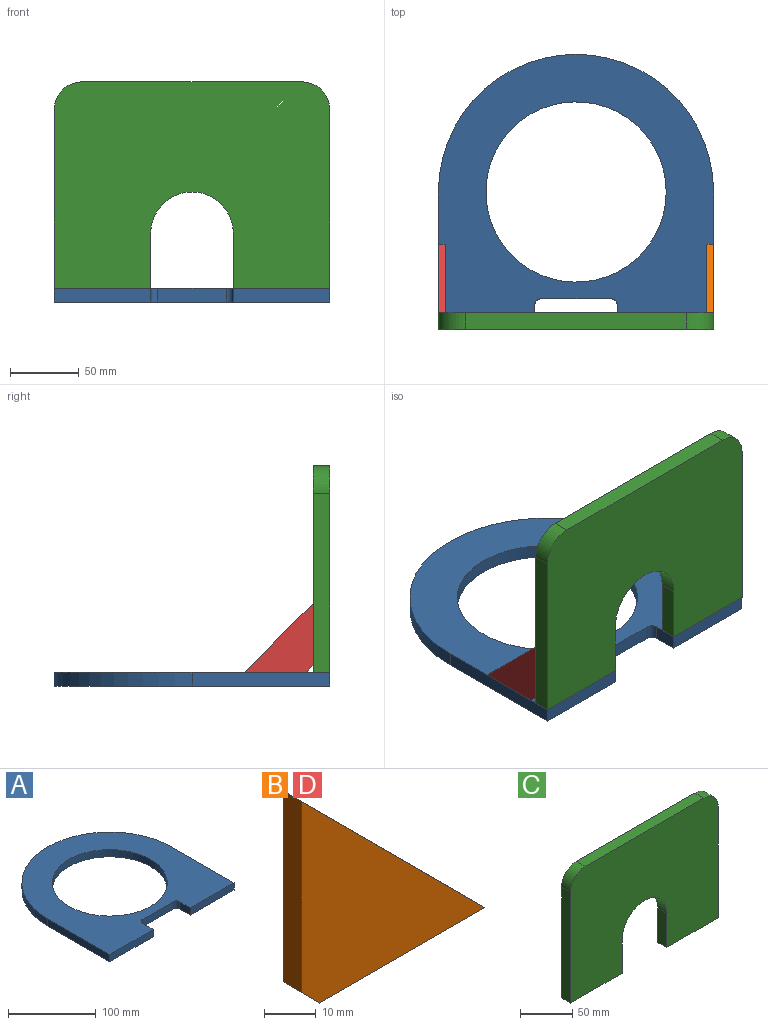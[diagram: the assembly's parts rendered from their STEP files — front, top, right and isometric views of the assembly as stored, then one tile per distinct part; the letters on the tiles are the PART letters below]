
ASSEMBLY  parts=4 mates=3
PART A: 13 faces, bbox 200x200x10 mm
  f0: plane 200x200mm, normal (0,0,1), area 20890.5mm2, adj f1,f2,f3,f4,f6,f7,f8,f9
  f1: plane 70x10mm, normal (0,-1,0), area 700mm2, adj f0,f3,f5,f8
  f2: plane 100x10mm, normal (-1,0,0), area 1000mm2, adj f0,f4,f5,f7
  f3: plane 100x10mm, normal (1,0,0), area 1000mm2, adj f0,f1,f5,f7
  f4: plane 70x10mm, normal (0,-1,0), area 700mm2, adj f0,f2,f5,f9
  f5: plane 200x200mm, normal (0,0,-1), area 20890.5mm2, adj f1,f2,f3,f4,f6,f7,f8,f9
  f6: cylinder r=65.5mm len=131mm, axis (0,0,1), area 4115.5mm2, adj f0,f5
  f7: cylinder r=100mm len=200mm, axis (0,0,-1), area 3141.6mm2, adj f0,f2,f3,f5
  f8: plane 17.5x10mm, normal (-1,0,0), area 175mm2, adj f0,f1,f5,f12
  f9: plane 17.5x10mm, normal (1,0,0), area 175mm2, adj f0,f4,f5,f10
  f10: cylinder r=5mm len=10mm, axis (0,0,-1), area 78.5mm2, adj f0,f5,f9,f11
  f11: plane 50x10mm, normal (0,-1,0), area 500mm2, adj f0,f5,f10,f12
  f12: cylinder r=5mm len=10mm, axis (0,0,-1), area 78.5mm2, adj f0,f5,f8,f11
PART B: 6 faces, bbox 50x5x50 mm
  f0: plane 45x5mm, normal (-1,0,0), area 225mm2, adj f1,f2,f4,f5
  f1: plane 50x50mm, normal (0,-1,0), area 1237.5mm2, adj f0,f3,f4,f5
  f2: plane 50x50mm, normal (0,1,0), area 1237.5mm2, adj f0,f3,f4,f5
  f3: plane 45x5mm, normal (0,0,-1), area 225mm2, adj f1,f2,f4,f5
  f4: plane 50x50mm, normal (0.71,0,0.71), area 353.6mm2, adj f0,f1,f2,f3
  f5: plane 5x5mm, normal (-0.71,0,-0.71), area 35.4mm2, adj f0,f1,f2,f3
PART C: 12 faces, bbox 200x12x150 mm
  f0: plane 70x12mm, normal (0,0,-1), area 840mm2, adj f2,f4,f5,f7
  f1: plane 130x12mm, normal (1,0,0), area 1560mm2, adj f3,f4,f5,f11
  f2: plane 130x12mm, normal (-1,0,0), area 1560mm2, adj f0,f4,f5,f10
  f3: plane 70x12mm, normal (0,0,-1), area 840mm2, adj f1,f4,f5,f8
  f4: plane 200x150mm, normal (0,-1,0), area 26014.6mm2, adj f0,f1,f2,f3,f6,f7,f8,f9
  f5: plane 200x150mm, normal (0,1,0), area 26014.6mm2, adj f0,f1,f2,f3,f6,f7,f8,f9
  f6: cylinder r=30mm len=60mm, axis (0,-1,0), area 1131mm2, adj f4,f5,f7,f8
  f7: plane 40x12mm, normal (1,0,0), area 480mm2, adj f0,f4,f5,f6
  f8: plane 40x12mm, normal (-1,0,0), area 480mm2, adj f3,f4,f5,f6
  f9: plane 160x12mm, normal (0,0,1), area 1920mm2, adj f4,f5,f10,f11
  f10: cylinder r=20mm len=20mm, axis (0,-1,0), area 377mm2, adj f2,f4,f5,f9
  f11: cylinder r=20mm len=20mm, axis (0,1,0), area 377mm2, adj f1,f4,f5,f9
PART D: same geometry as B
PLACE A t=(0,0,10)mm
PLACE B rot(axis=(0,0,1),90deg) t=(95,-88,10)mm
PLACE C t=(0,-88,60)mm
PLACE D rot(axis=(0,0,1),90deg) t=(-100,-88,10)mm
MATE fastened D.f3 <-> A.f0  axis (0,0,-1) through (-100,-38,10)mm
MATE fastened B.f3 <-> A.f0  axis (0,0,-1) through (100,-38,10)mm
MATE fastened C.f3 <-> A.f0  axis (0,0,1) through (100,-100,10)mm
